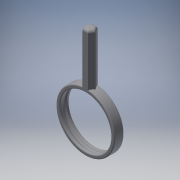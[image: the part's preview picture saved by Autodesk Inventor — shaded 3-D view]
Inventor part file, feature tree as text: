
AUTODESK INVENTOR PART (.ipt)
format: ipt  version: 2016 (Build 200138000, 138)  size: 199,680 bytes
history: native  units: mm
features: fillet x5, revolve x1, plane x1, extrude x1, sketch x1
ambient origin geometry x8: Origin, YZ Plane, XZ Plane, XY Plane, X Axis, Y Axis, Z Axis, Center Point
bodies: Solid1 (feature_tree)
feature tree (9):
  revolve  "Revolution1"  [1 undecoded]
  plane  "Work Plane1"
  extrude  "Extrusion1"  Depth=4.5mm
  fillet  "Fillet2"  Radius=7.0mm
  fillet  "Fillet3"  Radius=5.0mm
  fillet  "Fillet4"  [1 undecoded]
  fillet  "Fillet5"  Radius=50.0mm
  fillet  "Fillet6"  Radius=100.0mm
  sketch  "Sketch1"  dims[d0=50.0mm d1=9.0mm d2=5.0mm d3=7.0mm d4=5.0mm d5=90.0deg d6=50.0mm d8=100.0mm d9=0.0mm d11=2.0mm d12=2.0mm d13=2.0mm d14=1.0mm d15=18.0mm d16=4.5mm]
note: 2 required parameter values undecoded (feature->parameter linkage not recoverable at this tier; creation-order binding heuristic only, values carry confidence <= 0.55)